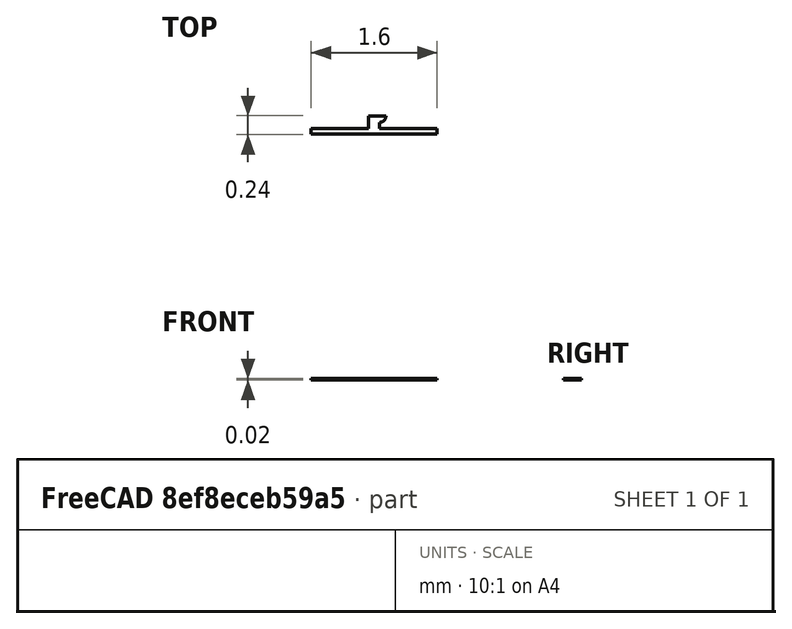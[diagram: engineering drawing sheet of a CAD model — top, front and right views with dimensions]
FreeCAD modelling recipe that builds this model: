
FCSTD DOCUMENT  (FreeCAD 0.17R12607 (Git))
Label: 1616 RGB LED Anode
License: CreativeCommons Attribution-ShareAlike
LicenseURL: http://creativecommons.org/licenses/by-sa/4.0/
objects: Sketcher::SketchObject×1, PartDesign::Pad×1, PartDesign::Body×1
note: 4 computed .brp shape members not serialized (recipe doc carries the construction recipe); baked Part::Feature solids carry a one-line shape summary decoded from their .brp

FEATURE [Sketcher::SketchObject] Sketch
  MapMode = 5
  Support = -> [XY_Plane]
  sketch-geometry (9):
    g0: LineSegment StartX=0.8 StartY=0.035 StartZ=0 EndX=0.8 EndY=-0.035 EndZ=0
    g1: LineSegment StartX=0.8 StartY=-0.035 StartZ=0 EndX=-0.8 EndY=-0.035 EndZ=0
    g2: LineSegment StartX=-0.8 StartY=-0.035 StartZ=0 EndX=-0.8 EndY=0.035 EndZ=0
    g3: LineSegment StartX=-0.07 StartY=0.035 StartZ=0 EndX=-0.07 EndY=0.195 EndZ=0
    g4: LineSegment StartX=-0.07 StartY=0.195 StartZ=0 EndX=0.15 EndY=0.195 EndZ=0
    g5: ArcOfCircle CenterX=0.07 CenterY=0.195 CenterZ=0 NormalX=0 NormalY=0 NormalZ=1 AngleXU=0 Radius=0.08 StartAngle=4.71239 EndAngle=6.28319
    g6: LineSegment StartX=0.07 StartY=0.115 StartZ=0 EndX=0.07 EndY=0.035 EndZ=0
    g7: LineSegment StartX=-0.8 StartY=0.035 StartZ=0 EndX=-0.07 EndY=0.035 EndZ=0
    g8: LineSegment StartX=0.07 StartY=0.035 StartZ=0 EndX=0.8 EndY=0.035 EndZ=0
  constraints (27):
    c: Coincident(g0,g1)
    c: Coincident(g1,g2)
    c: Horizontal(g1)
    c: Vertical(g0)
    c: Vertical(g2)
    c: Symmetric(g2,g0,g-2)
    c: Symmetric(g0,g0,g-1)
    c: DistanceX(g2,g0) = 1.6
    c: DistanceY(g0,g0) = 0.07
    c: Vertical(g3)
    c: Coincident(g3,g4)
    c: Horizontal(g4)
    c: PointOnObject(g5,g4)
    c: Coincident(g5,g4)
    c: Coincident(g6,g5)
    c: Vertical(g6)
    c: DistanceY(g3,g3) = 0.16
    c: Coincident(g7,g2)
    c: Coincident(g7,g3)
    c: Horizontal(g7)
    c: Coincident(g8,g6)
    c: Coincident(g8,g0)
    c: Horizontal(g8)
    c: Equal(g8,g7)
    c: Distance(g3,g6) = 0.14
    c: Perpendicular(g5,g6)
    c: DistanceX(g4,g4) = 0.22
FEATURE [PartDesign::Pad] Pad
  Length = 0.02
  Length2 = 100
  Profile = -> Sketch
  Type = 0
FEATURE [PartDesign::Body] Body
  Group = -> [Sketch,Pad]
  Origin = -> Origin
  Tip = -> Pad
